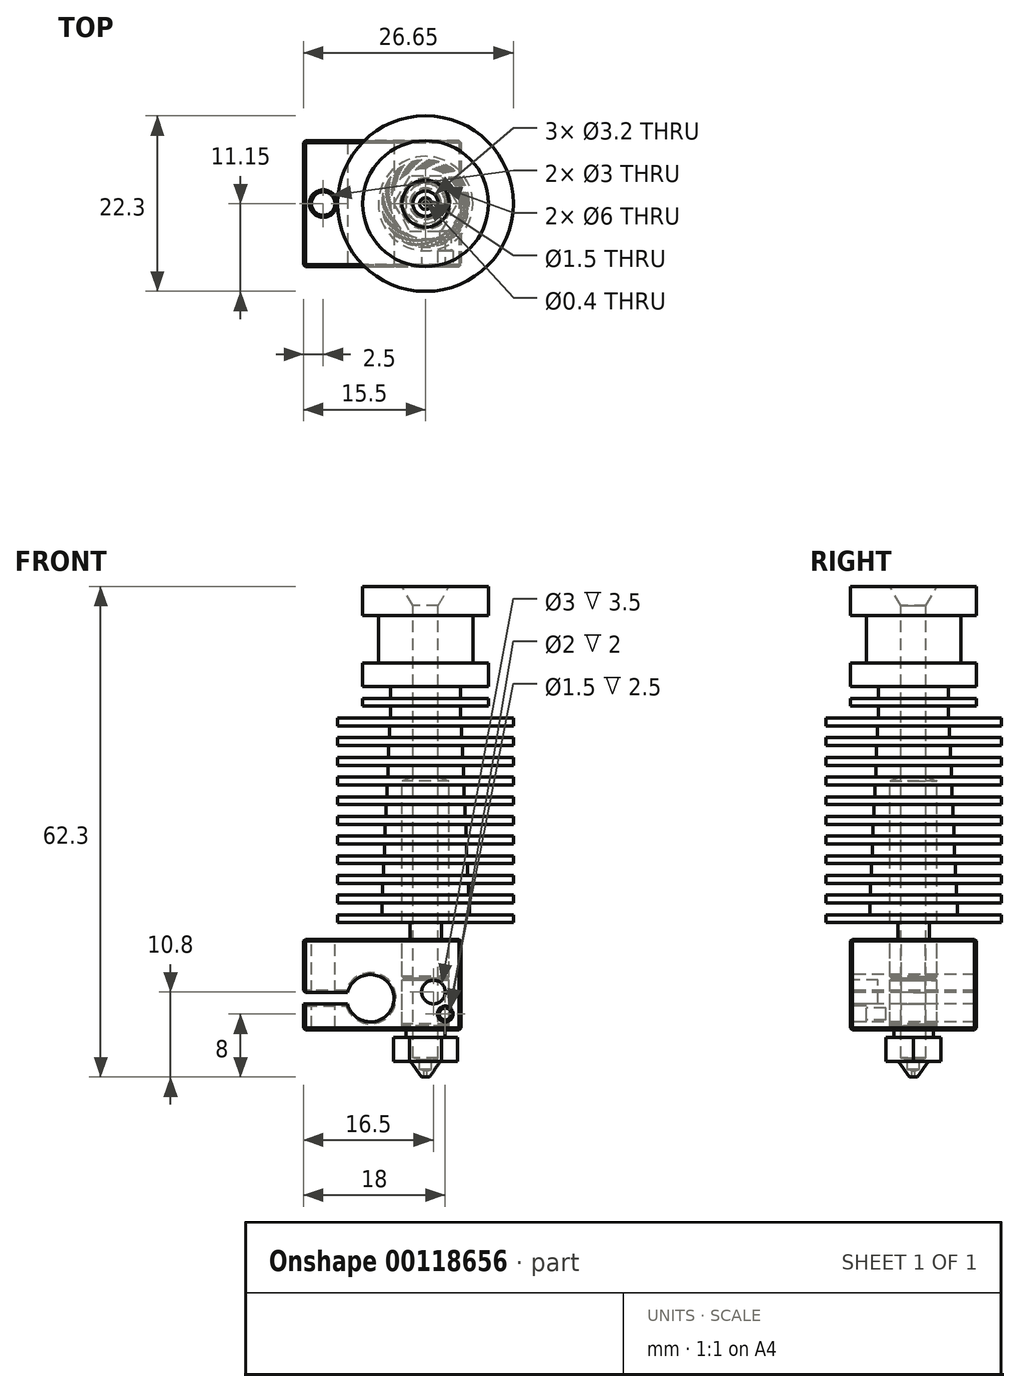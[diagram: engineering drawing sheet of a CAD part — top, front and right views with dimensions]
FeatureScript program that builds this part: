
annotation { "Feature Type Name" : "Feature", "Feature Type Description" : "" }
export const myFeature = defineFeature(function(context is Context, id is Id, definition is map)
    precondition{}
    {
        {
            var Q0;
            Q0=qCreatedBy(makeId("Front.planeOp"),FACE);
            var sketch = newSketch(context, id + "F0", { "sketchPlane" : qUnion([Q0])});
            skLineSegment(sketch, "E0", {"start": v(0, 0) * mm, "end": v(11.15, 0) * mm});
            skLineSegment(sketch, "E1", {"start": v(11.15, 0) * mm, "end": v(11.15, 1) * mm});
            skLineSegment(sketch, "E2", {"start": v(11.15, 1) * mm, "end": v(5.56, 1) * mm});
            skLineSegment(sketch, "E3", {"start": v(5.56, 1) * mm, "end": v(5.56, 2.5) * mm});
            skLineSegment(sketch, "E4", {"start": v(5.56, 2.5) * mm, "end": v(11.15, 2.5) * mm});
            skLineSegment(sketch, "E5", {"start": v(11.15, 2.5) * mm, "end": v(11.15, 3.5) * mm});
            skLineSegment(sketch, "E6", {"start": v(11.15, 3.5) * mm, "end": v(5.45, 3.5) * mm});
            skLineSegment(sketch, "E7", {"start": v(5.45, 3.5) * mm, "end": v(5.45, 5) * mm});
            skLineSegment(sketch, "E8", {"start": v(5.45, 5) * mm, "end": v(11.15, 5) * mm});
            skLineSegment(sketch, "E9", {"start": v(11.15, 5) * mm, "end": v(11.15, 6) * mm});
            skLineSegment(sketch, "E10", {"start": v(11.15, 6) * mm, "end": v(5.34, 6) * mm});
            skLineSegment(sketch, "E11", {"start": v(5.34, 6) * mm, "end": v(5.34, 7.5) * mm});
            skLineSegment(sketch, "E12", {"start": v(5.34, 7.5) * mm, "end": v(11.15, 7.5) * mm});
            skLineSegment(sketch, "E13", {"start": v(11.15, 7.5) * mm, "end": v(11.15, 8.5) * mm});
            skLineSegment(sketch, "E14", {"start": v(11.15, 8.5) * mm, "end": v(5.23, 8.5) * mm});
            skLineSegment(sketch, "E15", {"start": v(5.23, 8.5) * mm, "end": v(5.23, 10) * mm});
            skLineSegment(sketch, "E16", {"start": v(5.23, 10) * mm, "end": v(11.15, 10) * mm});
            skLineSegment(sketch, "E17", {"start": v(11.15, 10) * mm, "end": v(11.15, 11) * mm});
            skLineSegment(sketch, "E18", {"start": v(11.15, 11) * mm, "end": v(5.12, 11) * mm});
            skLineSegment(sketch, "E19", {"start": v(5.12, 11) * mm, "end": v(5.12, 12.5) * mm});
            skLineSegment(sketch, "E20", {"start": v(5.12, 12.5) * mm, "end": v(11.15, 12.5) * mm});
            skLineSegment(sketch, "E21", {"start": v(11.15, 12.5) * mm, "end": v(11.15, 13.5) * mm});
            skLineSegment(sketch, "E22", {"start": v(11.15, 13.5) * mm, "end": v(5.01, 13.5) * mm});
            skLineSegment(sketch, "E23", {"start": v(5.01, 13.5) * mm, "end": v(5.01, 15) * mm});
            skLineSegment(sketch, "E24", {"start": v(5.01, 15) * mm, "end": v(11.15, 15) * mm});
            skLineSegment(sketch, "E25", {"start": v(11.15, 15) * mm, "end": v(11.15, 16) * mm});
            skLineSegment(sketch, "E26", {"start": v(11.15, 16) * mm, "end": v(4.9, 16) * mm});
            skLineSegment(sketch, "E27", {"start": v(4.9, 16) * mm, "end": v(4.9, 17.5) * mm});
            skLineSegment(sketch, "E28", {"start": v(4.9, 17.5) * mm, "end": v(11.15, 17.5) * mm});
            skLineSegment(sketch, "E29", {"start": v(11.15, 17.5) * mm, "end": v(11.15, 18.5) * mm});
            skLineSegment(sketch, "E30", {"start": v(11.15, 18.5) * mm, "end": v(4.8, 18.5) * mm});
            skLineSegment(sketch, "E31", {"start": v(4.8, 18.5) * mm, "end": v(4.8, 20) * mm});
            skLineSegment(sketch, "E32", {"start": v(4.8, 20) * mm, "end": v(11.15, 20) * mm});
            skLineSegment(sketch, "E33", {"start": v(11.15, 20) * mm, "end": v(11.15, 21) * mm});
            skLineSegment(sketch, "E34", {"start": v(5.6, 0) * mm, "end": v(4.46, 26) * mm, "construction": true});
            skLineSegment(sketch, "E35", {"start": v(11.15, 21) * mm, "end": v(4.68, 21) * mm});
            skLineSegment(sketch, "E36", {"start": v(4.68, 21) * mm, "end": v(4.68, 22.5) * mm});
            skLineSegment(sketch, "E37", {"start": v(4.68, 22.5) * mm, "end": v(11.15, 22.5) * mm});
            skLineSegment(sketch, "E38", {"start": v(11.15, 22.5) * mm, "end": v(11.15, 23.5) * mm});
            skLineSegment(sketch, "E39", {"start": v(11.15, 23.5) * mm, "end": v(4.57, 23.5) * mm});
            skLineSegment(sketch, "E40", {"start": v(4.57, 23.5) * mm, "end": v(4.57, 25) * mm});
            skLineSegment(sketch, "E41", {"start": v(4.57, 25) * mm, "end": v(11.15, 25) * mm});
            skLineSegment(sketch, "E42", {"start": v(11.15, 25) * mm, "end": v(11.15, 26) * mm});
            skLineSegment(sketch, "E43", {"start": v(11.15, 26) * mm, "end": v(4.46, 26) * mm});
            skLineSegment(sketch, "E44", {"start": v(4.46, 26) * mm, "end": v(4.46, 27.5) * mm});
            skLineSegment(sketch, "E45", {"start": v(4.46, 27.5) * mm, "end": v(8, 27.5) * mm});
            skLineSegment(sketch, "E46", {"start": v(8, 27.5) * mm, "end": v(8, 28.5) * mm});
            skLineSegment(sketch, "E47", {"start": v(8, 28.5) * mm, "end": v(4.46, 28.5) * mm});
            skLineSegment(sketch, "E48", {"start": v(4.46, 30) * mm, "end": v(8, 30) * mm});
            skLineSegment(sketch, "E49", {"start": v(8, 30) * mm, "end": v(8, 33) * mm});
            skLineSegment(sketch, "E50", {"start": v(8, 33) * mm, "end": v(6, 33) * mm});
            skLineSegment(sketch, "E51", {"start": v(6, 33) * mm, "end": v(6, 39) * mm});
            skLineSegment(sketch, "E52", {"start": v(6, 39) * mm, "end": v(8, 39) * mm});
            skLineSegment(sketch, "E53", {"start": v(8, 39) * mm, "end": v(8, 42.7) * mm});
            skLineSegment(sketch, "E54", {"start": v(8, 42.7) * mm, "end": v(3, 42.7) * mm});
            skLineSegment(sketch, "E55", {"start": v(4.46, 28.5) * mm, "end": v(4.46, 30) * mm});
            skLineSegment(sketch, "E56", {"start": v(0, 42.7) * mm, "end": v(0, 0) * mm, "construction": true});
            skLineSegment(sketch, "E57", {"start": v(3, 42.7) * mm, "end": v(1.6, 40.28) * mm});
            skLineSegment(sketch, "E58", {"start": v(1.6, 40.28) * mm, "end": v(1.6, 18.5) * mm});
            skLineSegment(sketch, "E59", {"start": v(1.6, 18.5) * mm, "end": v(3, 18) * mm});
            skLineSegment(sketch, "E60", {"start": v(3, 18) * mm, "end": v(3, 0) * mm});
            skLineSegment(sketch, "E61", {"start": v(1.6, 18.5) * mm, "end": v(1.6, 0) * mm});
            skLineSegment(sketch, "E62", {"start": v(2, 0) * mm, "end": v(2, -2.1) * mm});
            skLineSegment(sketch, "E63", {"start": v(2, -2.1) * mm, "end": v(3, -2.1) * mm});
            skLineSegment(sketch, "E64", {"start": v(3, -2.1) * mm, "end": v(3, -6.85) * mm});
            skLineSegment(sketch, "E65", {"start": v(2.75, -7.1) * mm, "end": v(1.6, -7.1) * mm});
            skLineSegment(sketch, "E66", {"start": v(1.6, 0) * mm, "end": v(1.6, -7.1) * mm});
            skLineSegment(sketch, "E67", {"start": v(1.6, -7.1) * mm, "end": v(1.6, -7.1) * mm});
            skLineSegment(sketch, "E68", {"start": v(2.75, -7.1) * mm, "end": v(3, -6.85) * mm});
            skLineSegment(sketch, "E69", {"start": v(2.75, -7.1) * mm, "end": v(3, -7.35) * mm});
            skLineSegment(sketch, "E70", {"start": v(3, -7.35) * mm, "end": v(3, -12.85) * mm});
            skLineSegment(sketch, "E71", {"start": v(3, -12.85) * mm, "end": v(2.75, -13.1) * mm});
            skLineSegment(sketch, "E72", {"start": v(2.75, -13.1) * mm, "end": v(2.5, -13.1) * mm});
            skLineSegment(sketch, "E73", {"start": v(2.5, -13.1) * mm, "end": v(2.5, -14.6) * mm});
            skLineSegment(sketch, "E74", {"start": v(2.5, -14.6) * mm, "end": v(5, -14.6) * mm});
            skLineSegment(sketch, "E75", {"start": v(5, -14.6) * mm, "end": v(5, -17.6) * mm});
            skLineSegment(sketch, "E76", {"start": v(5, -17.6) * mm, "end": v(1.9, -17.6) * mm});
            skLineSegment(sketch, "E77", {"start": v(1.9, -17.6) * mm, "end": v(0.5, -19.6) * mm});
            skLineSegment(sketch, "E78", {"start": v(0.5, -19.6) * mm, "end": v(0.2, -19.6) * mm});
            skLineSegment(sketch, "E79", {"start": v(0.2, -19.6) * mm, "end": v(0.2, -18.8) * mm});
            skLineSegment(sketch, "E80", {"start": v(0.2, -18.8) * mm, "end": v(0.75, -18.63) * mm});
            skLineSegment(sketch, "E81", {"start": v(0.75, -18.63) * mm, "end": v(0.75, -17.46) * mm});
            skLineSegment(sketch, "E82", {"start": v(0.75, -17.46) * mm, "end": v(1.6, -17.2) * mm});
            skLineSegment(sketch, "E83", {"start": v(1.6, -17.2) * mm, "end": v(1.6, -7.35) * mm});
            skLineSegment(sketch, "E84", {"start": v(1.6, -7.35) * mm, "end": v(1.85, -7.1) * mm});
            skSolve(sketch);
        }
        {
            var Q0;
            {var subQ0=sQuery(id+"F0.wireOp",EDGE,"E1");Q0=makeQuery(id+"F0.imprint","IMPRINT",FACE,{"disambiguationData":[TD([[makeQuery(id+"F0.imprint","IMPRINT",EDGE,{"derivedFrom":subQ0}),1.0]])]});}
            var Q1;
            Q1=sQuery(id+"F0.wireOp",EDGE,"E56");
            revolve(context, id + "F1", {"entities" : qUnion([Q0]), "axis" : qUnion([Q1]), "revolveType" : RevolveType.FULL});
        }
        {
            var Q0;
            Q0=makeQuery(id+"F0.imprint","IMPRINT",FACE,{"disambiguationData":[TD([[makeQuery(id+"F0.imprint","IMPRINT",EDGE,{"derivedFrom":sQuery(id+"F0.wireOp",EDGE,"E59")}),-1.0]])]});
            var Q1;
            {var subQ0=sQuery(id+"F0.wireOp",EDGE,"E62");Q1=makeQuery(id+"F0.imprint","IMPRINT",FACE,{"disambiguationData":[TD([[makeQuery(id+"F0.imprint","IMPRINT",EDGE,{"derivedFrom":subQ0}),-1.0]])]});}
            var Q2;
            Q2=sQuery(id+"F0.wireOp",EDGE,"E56");
            revolve(context, id + "F2", {"entities" : qUnion([Q0, Q1]), "axis" : qUnion([Q2]), "revolveType" : RevolveType.FULL});
        }
        {
            var Q0;
            {var subQ0=sQuery(id+"F0.wireOp",EDGE,"E69");Q0=makeQuery(id+"F0.imprint","IMPRINT",FACE,{"disambiguationData":[TD([[makeQuery(id+"F0.imprint","IMPRINT",EDGE,{"derivedFrom":subQ0}),-1.0]])]});}
            var Q1;
            Q1=sQuery(id+"F0.wireOp",EDGE,"E56");
            revolve(context, id + "F3", {"entities" : qUnion([Q0]), "axis" : qUnion([Q1]), "revolveType" : RevolveType.FULL});
        }
        {
            var Q0;
            Q0=makeQuery(id+"F3.opRevolve","SWEPT_FACE",FACE,{"disambiguationData":[OSD([sQuery(id+"F0.wireOp",EDGE,"E76")])]});
            var sketch = newSketch(context, id + "F4", { "sketchPlane" : qUnion([Q0])});
            skCircle(sketch, "E85.cCircle", {"center": v(0, 0) * mm, "radius": 3.5 * mm, "construction": true});
            skLineSegment(sketch, "E85.0", {"start": v(-2.02, 3.5) * mm, "end": v(2.02, 3.5) * mm});
            skLineSegment(sketch, "E85.1", {"start": v(2.02, 3.5) * mm, "end": v(4.04, 0) * mm});
            skLineSegment(sketch, "E85.2", {"start": v(4.04, 0) * mm, "end": v(2.02, -3.5) * mm});
            skLineSegment(sketch, "E85.3", {"start": v(2.02, -3.5) * mm, "end": v(-2.02, -3.5) * mm});
            skLineSegment(sketch, "E85.4", {"start": v(-2.02, -3.5) * mm, "end": v(-4.04, 0) * mm});
            skLineSegment(sketch, "E85.5", {"start": v(-4.04, 0) * mm, "end": v(-2.02, 3.5) * mm});
            skPoint(sketch, "E85.0.midPoint", {"position": v(0, 3.5) * mm});
            skSolve(sketch);
        }
        {
            var Q0;
            Q0=makeQuery(id+"F4.imprint","IMPRINT",FACE,{"disambiguationData":[TD([[makeQuery(id+"F4.imprint","IMPRINT",EDGE,{"derivedFrom":sQuery(id+"F4.wireOp",EDGE,"E85.0")}),1.0]])]});
            var Q1;
            Q1=makeQuery(id+"F3.opRevolve","SWEPT_FACE",FACE,{"disambiguationData":[OSD([sQuery(id+"F0.wireOp",EDGE,"E74")])]});
            extrude(context, id + "F5", {"entities" : qUnion([Q0]), "operationType" : NewBodyOperationType.REMOVE, "endBound" : BoundingType.UP_TO_SURFACE, "oppositeDirection" : true, "endBoundEntityFace" : qUnion([Q1]), "depth" : 25 * mm});
        }
        {
            var Q0;
            Q0=makeQuery(id+"F2.opRevolve","SWEPT_FACE",FACE,{"disambiguationData":[OSD([sQuery(id+"F0.wireOp",EDGE,"E63")])]});
            var sketch = newSketch(context, id + "F6", { "sketchPlane" : qUnion([Q0])});
            skPoint(sketch, "E86", {"position": v(0, 0) * mm});
            skLineSegment(sketch, "E87.bottom", {"start": v(-15.5, 8) * mm, "end": v(4.5, 8) * mm});
            skLineSegment(sketch, "E87.top", {"start": v(-15.5, -8) * mm, "end": v(4.5, -8) * mm});
            skLineSegment(sketch, "E87.left", {"start": v(-15.5, 8) * mm, "end": v(-15.5, -8) * mm});
            skLineSegment(sketch, "E87.right", {"start": v(4.5, 8) * mm, "end": v(4.5, -8) * mm});
            skCircle(sketch, "E88", {"center": v(-13, 0) * mm, "radius": 1.5 * mm});
            skCircle(sketch, "E89.0", {"center": v(0, 0) * mm, "radius": 3 * mm});
            skSolve(sketch);
        }
        {
            var Q0;
            Q0=makeQuery(id+"F6.imprint","IMPRINT",FACE,{"disambiguationData":[TD([[makeQuery(id+"F6.imprint","IMPRINT",EDGE,{"derivedFrom":sQuery(id+"F6.wireOp",EDGE,"E87.bottom")}),-1.0]])]});
            extrude(context, id + "F7", {"entities" : qUnion([Q0]), "oppositeDirection" : true, "depth" : 11.5 * mm});
        }
        {
            var Q0;
            Q0=makeQuery(id+"F7.opExtrude","SWEPT_FACE",FACE,{"disambiguationData":[OSD([sQuery(id+"F6.wireOp",EDGE,"E87.top")])]});
            var sketch = newSketch(context, id + "F8", { "sketchPlane" : qUnion([Q0])});
            skArc(sketch, "E90", {"start": v(-9.9, -10.35) * mm, "mid": v(-4, -9.6) * mm, "end": v(-9.9, -8.85) * mm});
            skCircle(sketch, "E91", {"center": v(1, -8.8) * mm, "radius": 1.5 * mm});
            skCircle(sketch, "E92", {"center": v(2.5, -11.6) * mm, "radius": 1 * mm});
            skCircle(sketch, "E93", {"center": v(2.5, -11.6) * mm, "radius": 0.75 * mm});
            skLineSegment(sketch, "E94", {"start": v(-9.9, -10.35) * mm, "end": v(-15.5, -10.35) * mm});
            skLineSegment(sketch, "E95", {"start": v(-15.5, -8.85) * mm, "end": v(-9.9, -8.85) * mm});
            skSolve(sketch);
        }
        {
            var Q0;
            Q0=makeQuery(id+"F8.imprint","IMPRINT",FACE,{"disambiguationData":[TD([[makeQuery(id+"F8.imprint","IMPRINT",EDGE,{"derivedFrom":sQuery(id+"F8.wireOp",EDGE,"E90")}),1.0]])]});
            extrude(context, id + "F9", {"entities" : qUnion([Q0]), "operationType" : NewBodyOperationType.REMOVE, "endBound" : BoundingType.THROUGH_ALL, "oppositeDirection" : true, "depth" : 25 * mm});
        }
        {
            var Q0;
            Q0=makeQuery(id+"F8.imprint","IMPRINT",FACE,{"disambiguationData":[TD([[makeQuery(id+"F8.imprint","IMPRINT",EDGE,{"derivedFrom":sQuery(id+"F8.wireOp",EDGE,"E91")}),1.0]])]});
            extrude(context, id + "F10", {"entities" : qUnion([Q0]), "operationType" : NewBodyOperationType.REMOVE, "oppositeDirection" : true, "depth" : 3.5 * mm});
        }
        {
            var Q0;
            Q0=makeQuery(id+"F8.imprint","IMPRINT",FACE,{"disambiguationData":[TD([[makeQuery(id+"F8.imprint","IMPRINT",EDGE,{"derivedFrom":sQuery(id+"F8.wireOp",EDGE,"E93")}),1.0]])]});
            var Q1;
            Q1=sQuery(id+"F8.wireOp",EDGE,"E93");
            extrude(context, id + "F11", {"entities" : qUnion([Q0]), "operationType" : NewBodyOperationType.REMOVE, "surfaceEntities" : qUnion([Q1]), "oppositeDirection" : true, "depth" : 4.5 * mm});
        }
        {
            var Q0;
            Q0=makeQuery(id+"F8.imprint","IMPRINT",FACE,{"disambiguationData":[TD([[makeQuery(id+"F8.imprint","IMPRINT",EDGE,{"derivedFrom":sQuery(id+"F8.wireOp",EDGE,"E92")}),1.0]])]});
            extrude(context, id + "F12", {"entities" : qUnion([Q0]), "operationType" : NewBodyOperationType.REMOVE, "oppositeDirection" : true, "depth" : 2 * mm});
        }
        {
            var Q0;
            {var subQ0=sQuery(id+"F6.wireOp",EDGE,"E87.left");var subQ1=sQuery(id+"F6.wireOp",EDGE,"E87.top");Q0=makeQuery(id+"F9.boolean.opBoolean","SPLIT",EDGE,{"disambiguationData":[TD([makeQuery(id+"F9.opExtrude","SWEPT_FACE",FACE,{"disambiguationData":[OSD([sQuery(id+"F8.wireOp",EDGE,"E95")])]})])],"derivedFrom":makeQuery(id+"F7.opExtrude","SWEPT_EDGE",EDGE,{"disambiguationData":[OSD([subQ1,subQ0])]})});}
            var Q1;
            Q1=makeQuery(id+"F7.opExtrude","CAP_EDGE",EDGE,{"disambiguationData":[OSD([sQuery(id+"F6.wireOp",EDGE,"E87.top")])],"isStart":true});
            var Q2;
            Q2=makeQuery(id+"F7.opExtrude","SWEPT_EDGE",EDGE,{"disambiguationData":[OSD([sQuery(id+"F6.wireOp",EDGE,"E87.top"),sQuery(id+"F6.wireOp",EDGE,"E87.right")])]});
            var Q3;
            Q3=makeQuery(id+"F7.opExtrude","CAP_EDGE",EDGE,{"disambiguationData":[OSD([sQuery(id+"F6.wireOp",EDGE,"E87.top")])],"isStart":false});
            var Q4;
            Q4=makeQuery(id+"F9.boolean.opBoolean","COPY",EDGE,{"derivedFrom":makeQuery(id+"F9.opExtrude","SWEPT_EDGE",EDGE,{"disambiguationData":[OSD([sQuery(id+"F6.wireOp",EDGE,"E87.top"),sQuery(id+"F6.wireOp",EDGE,"E87.left"),sQuery(id+"F8.wireOp",EDGE,"E94")])]})});
            var Q5;
            Q5=makeQuery(id+"F9.boolean.opBoolean","COPY",EDGE,{"derivedFrom":makeQuery(id+"F9.opExtrude","SWEPT_EDGE",EDGE,{"disambiguationData":[OSD([sQuery(id+"F6.wireOp",EDGE,"E87.top"),sQuery(id+"F6.wireOp",EDGE,"E87.left"),sQuery(id+"F8.wireOp",EDGE,"E95")])]})});
            var Q6;
            Q6=makeQuery(id+"F7.opExtrude","CAP_EDGE",EDGE,{"disambiguationData":[OSD([sQuery(id+"F6.wireOp",EDGE,"E87.left")])],"isStart":false});
            var Q7;
            Q7=makeQuery(id+"F7.opExtrude","CAP_EDGE",EDGE,{"disambiguationData":[OSD([sQuery(id+"F6.wireOp",EDGE,"E87.left")])],"isStart":true});
            var Q8;
            {var subQ0=sQuery(id+"F6.wireOp",EDGE,"E87.bottom");var subQ1=sQuery(id+"F6.wireOp",EDGE,"E87.left");Q8=makeQuery(id+"F9.boolean.opBoolean","SPLIT",EDGE,{"disambiguationData":[TD([makeQuery(id+"F9.opExtrude","SWEPT_FACE",FACE,{"disambiguationData":[OSD([sQuery(id+"F8.wireOp",EDGE,"E95")])]})])],"derivedFrom":makeQuery(id+"F7.opExtrude","SWEPT_EDGE",EDGE,{"disambiguationData":[OSD([subQ0,subQ1])]})});}
            var Q9;
            {var subQ0=sQuery(id+"F6.wireOp",EDGE,"E87.bottom");var subQ1=sQuery(id+"F6.wireOp",EDGE,"E87.left");Q9=makeQuery(id+"F9.boolean.opBoolean","SPLIT",EDGE,{"disambiguationData":[TD([makeQuery(id+"F9.opExtrude","SWEPT_FACE",FACE,{"disambiguationData":[OSD([sQuery(id+"F8.wireOp",EDGE,"E94")])]})])],"derivedFrom":makeQuery(id+"F7.opExtrude","SWEPT_EDGE",EDGE,{"disambiguationData":[OSD([subQ0,subQ1])]})});}
            var Q10;
            Q10=makeQuery(id+"F9.boolean.opBoolean","INTERSECT",EDGE,{"derivedFrom":[makeQuery(id+"F7.opExtrude","SWEPT_FACE",FACE,{"disambiguationData":[OSD([sQuery(id+"F6.wireOp",EDGE,"E87.bottom")])]}),makeQuery(id+"F9.opExtrude","SWEPT_FACE",FACE,{"disambiguationData":[OSD([sQuery(id+"F8.wireOp",EDGE,"E95")])]})]});
            var Q11;
            Q11=makeQuery(id+"F9.boolean.opBoolean","INTERSECT",EDGE,{"derivedFrom":[makeQuery(id+"F7.opExtrude","SWEPT_FACE",FACE,{"disambiguationData":[OSD([sQuery(id+"F6.wireOp",EDGE,"E87.bottom")])]}),makeQuery(id+"F9.opExtrude","SWEPT_FACE",FACE,{"disambiguationData":[OSD([sQuery(id+"F8.wireOp",EDGE,"E94")])]})]});
            var Q12;
            Q12=makeQuery(id+"F9.boolean.opBoolean","INTERSECT",EDGE,{"derivedFrom":[makeQuery(id+"F7.opExtrude","SWEPT_FACE",FACE,{"disambiguationData":[OSD([sQuery(id+"F6.wireOp",EDGE,"E87.bottom")])]}),makeQuery(id+"F9.opExtrude","SWEPT_FACE",FACE,{"disambiguationData":[OSD([sQuery(id+"F8.wireOp",EDGE,"E90")])]})]});
            var Q13;
            Q13=makeQuery(id+"F7.opExtrude","CAP_EDGE",EDGE,{"disambiguationData":[OSD([sQuery(id+"F6.wireOp",EDGE,"E87.bottom")])],"isStart":true});
            var Q14;
            Q14=makeQuery(id+"F7.opExtrude","SWEPT_EDGE",EDGE,{"disambiguationData":[OSD([sQuery(id+"F6.wireOp",EDGE,"E87.bottom"),sQuery(id+"F6.wireOp",EDGE,"E87.right")])]});
            var Q15;
            Q15=makeQuery(id+"F7.opExtrude","CAP_EDGE",EDGE,{"disambiguationData":[OSD([sQuery(id+"F6.wireOp",EDGE,"E87.bottom")])],"isStart":false});
            var Q16;
            Q16=makeQuery(id+"F7.opExtrude","CAP_EDGE",EDGE,{"disambiguationData":[OSD([sQuery(id+"F6.wireOp",EDGE,"E88")])],"isStart":false});
            var Q17;
            Q17=makeQuery(id+"F7.opExtrude","CAP_EDGE",EDGE,{"disambiguationData":[OSD([sQuery(id+"F6.wireOp",EDGE,"E89.0")])],"isStart":false});
            var Q18;
            Q18=makeQuery(id+"F7.opExtrude","CAP_EDGE",EDGE,{"disambiguationData":[OSD([sQuery(id+"F6.wireOp",EDGE,"E87.right")])],"isStart":false});
            var Q19;
            Q19=makeQuery(id+"F7.opExtrude","CAP_EDGE",EDGE,{"disambiguationData":[OSD([sQuery(id+"F6.wireOp",EDGE,"E87.right")])],"isStart":true});
            var Q20;
            {var subQ0=sQuery(id+"F6.wireOp",EDGE,"E87.left");var subQ1=sQuery(id+"F6.wireOp",EDGE,"E87.top");Q20=makeQuery(id+"F9.boolean.opBoolean","SPLIT",EDGE,{"disambiguationData":[TD([makeQuery(id+"F9.opExtrude","SWEPT_FACE",FACE,{"disambiguationData":[OSD([sQuery(id+"F8.wireOp",EDGE,"E94")])]})])],"derivedFrom":makeQuery(id+"F7.opExtrude","SWEPT_EDGE",EDGE,{"disambiguationData":[OSD([subQ1,subQ0])]})});}
            var Q21;
            Q21=makeQuery(id+"F7.opExtrude","CAP_EDGE",EDGE,{"disambiguationData":[OSD([sQuery(id+"F6.wireOp",EDGE,"E88")])],"isStart":true});
            var Q22;
            Q22=makeQuery(id+"F7.opExtrude","CAP_EDGE",EDGE,{"disambiguationData":[OSD([sQuery(id+"F6.wireOp",EDGE,"E89.0")])],"isStart":true});
            var Q23;
            Q23=makeQuery(id+"F10.boolean.opBoolean","COPY",EDGE,{"derivedFrom":makeQuery(id+"F10.opExtrude","CAP_EDGE",EDGE,{"disambiguationData":[OSD([sQuery(id+"F8.wireOp",EDGE,"E91")])],"isStart":true})});
            var Q24;
            Q24=makeQuery(id+"F12.boolean.opBoolean","COPY",EDGE,{"derivedFrom":makeQuery(id+"F12.opExtrude","CAP_EDGE",EDGE,{"disambiguationData":[OSD([sQuery(id+"F8.wireOp",EDGE,"E92")])],"isStart":true})});
            var Q25;
            Q25=makeQuery(id+"F9.boolean.opBoolean","COPY",EDGE,{"derivedFrom":makeQuery(id+"F9.opExtrude","CAP_EDGE",EDGE,{"disambiguationData":[OSD([sQuery(id+"F8.wireOp",EDGE,"E90")])],"isStart":true})});
            chamfer(context, id + "F13", {"entities" : qUnion([Q0, Q1, Q2, Q3, Q4, Q5, Q6, Q7, Q8, Q9, Q10, Q11, Q12, Q13, Q14, Q15, Q16, Q17, Q18, Q19, Q20, Q21, Q22, Q23, Q24, Q25]), "width" : .25 * mm, "tangentPropagation" : true});
        }
    });
